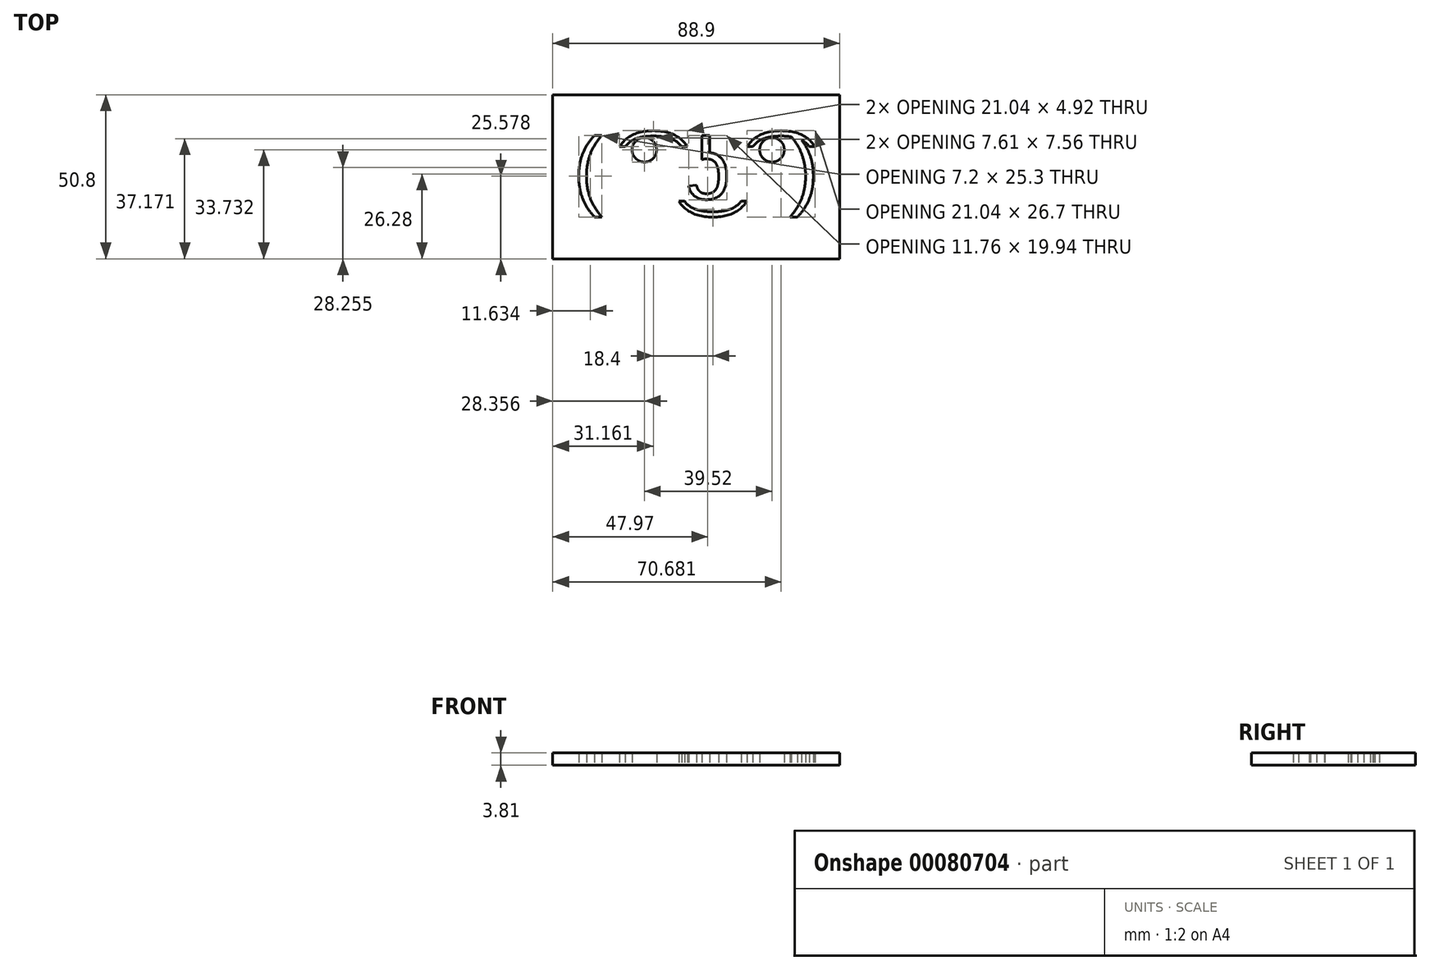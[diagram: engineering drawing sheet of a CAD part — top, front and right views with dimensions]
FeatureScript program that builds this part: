
annotation { "Feature Type Name" : "Feature", "Feature Type Description" : "" }
export const myFeature = defineFeature(function(context is Context, id is Id, definition is map)
    precondition{}
    {
        {
            var Q0;
            Q0=qCreatedBy(makeId("Top.planeOp"),FACE);
            var sketch = newSketch(context, id + "F0", { "sketchPlane" : qUnion([Q0])});
            skLineSegment(sketch, "E0.bottom", {"start": v(44.45, -25.4) * mm, "end": v(-44.45, -25.4) * mm});
            skLineSegment(sketch, "E0.top", {"start": v(44.45, 25.4) * mm, "end": v(-44.45, 25.4) * mm});
            skLineSegment(sketch, "E0.left", {"start": v(44.45, -25.4) * mm, "end": v(44.45, 25.4) * mm});
            skLineSegment(sketch, "E0.right", {"start": v(-44.45, -25.4) * mm, "end": v(-44.45, 25.4) * mm});
            skPoint(sketch, "E0.middle", {"position": v(0, 0) * mm});
            skText(sketch, "E1", { "text": "( ͡° ͜ʖ ͡°)", "fontName": "Arimo-Regular.ttf"});
            const initialGuessF0  = {"E1": [-0.0381, -0.00685, 1, 0, 0.01955]};
            skSetInitialGuess(sketch, initialGuessF0);
            skSolve(sketch);
        }
        {
            var Q0;
            Q0=makeQuery(id+"F0.imprint","IMPRINT",FACE,{"disambiguationData":[TD([[makeQuery(id+"F0.imprint","IMPRINT",EDGE,{"derivedFrom":sQuery(id+"F0.wireOp",EDGE,"E0.bottom")}),-1.0]])]});
            extrude(context, id + "F1", {"entities" : qUnion([Q0]), "depth" : 3.8 * mm});
        }
    });
